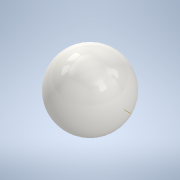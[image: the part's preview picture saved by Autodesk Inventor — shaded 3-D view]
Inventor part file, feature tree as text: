
AUTODESK INVENTOR PART (.ipt)
format: ipt  version: 2022.1 (Build 261234000, 234)  size: 121,344 bytes
history: native  units: mm
features: other x1, revolve x1, sketch x1
ambient origin geometry x8: Origin, YZ Plane, XZ Plane, XY Plane, X Axis, Y Axis, Z Axis, Center Point
bodies: Body1 (feature_tree)
feature tree (3):
  other  "Sólido1"
  revolve  "Revolución1"  Angle=90.0deg
  sketch  "Boceto1"  dims[d1=15.0mm d2=90.0deg]
